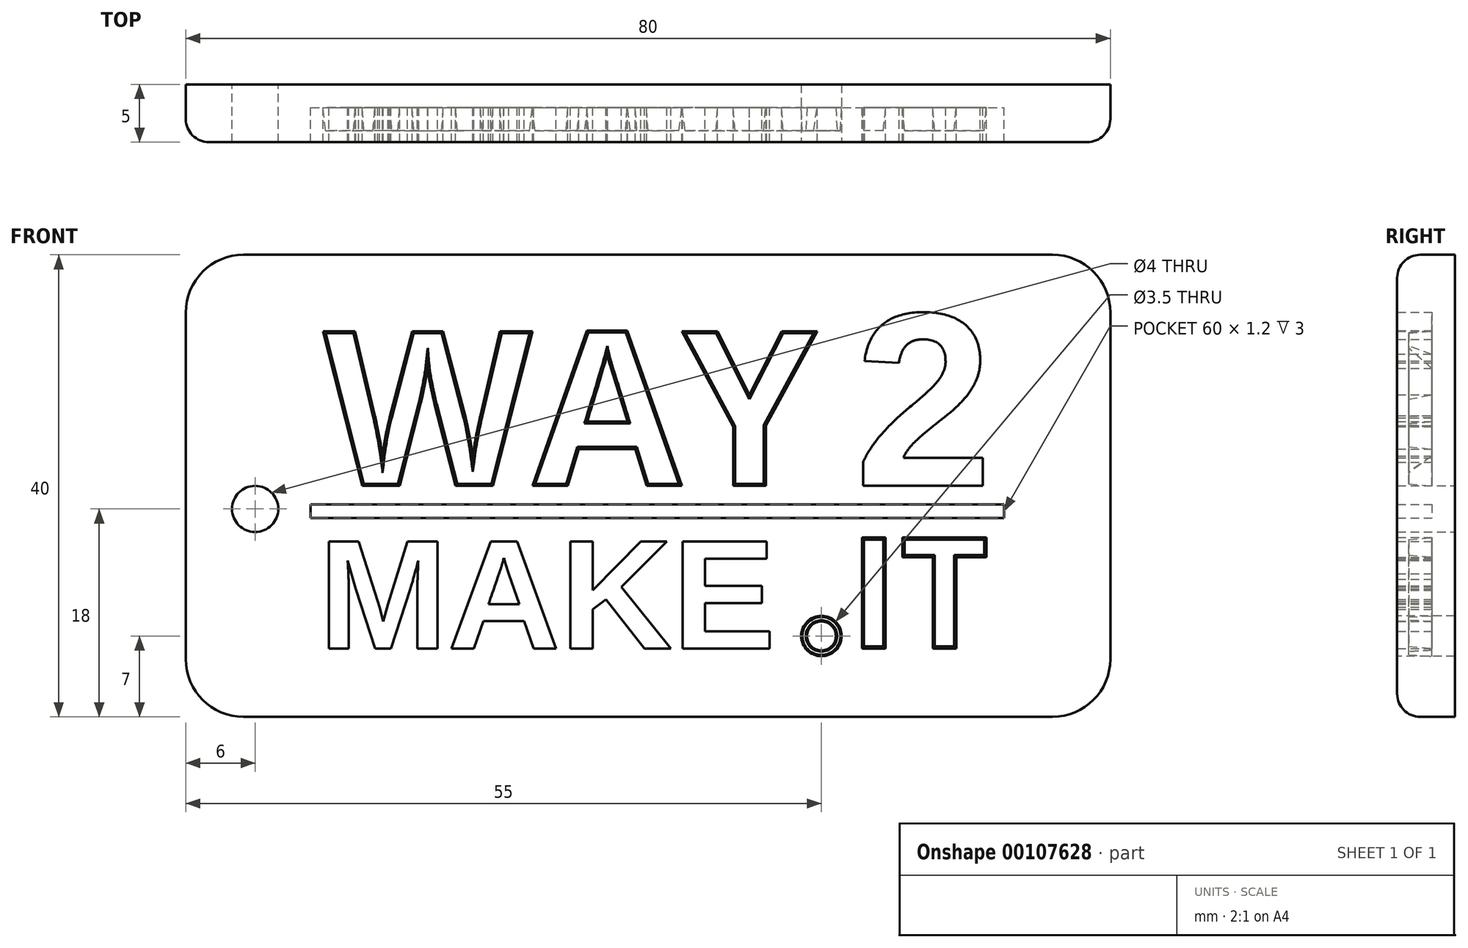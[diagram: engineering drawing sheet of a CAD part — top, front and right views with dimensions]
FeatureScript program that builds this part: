
annotation { "Feature Type Name" : "Feature", "Feature Type Description" : "" }
export const myFeature = defineFeature(function(context is Context, id is Id, definition is map)
    precondition{}
    {
        {
            var Q0;
            Q0=qCreatedBy(makeId("Front.planeOp"),FACE);
            var sketch = newSketch(context, id + "F0", { "sketchPlane" : qUnion([Q0])});
            skText(sketch, "E0", { "text": "WAY", "fontName": "OpenSans-Bold.ttf"});
            skText(sketch, "E1", { "text": "2", "fontName": "Arimo-Bold.ttf"});
            skText(sketch, "E2", { "text": "MAKE", "fontName": "Arimo-Bold.ttf"});
            skText(sketch, "E3", { "text": ".IT", "fontName": "OpenSans-Bold.ttf"});
            skLineSegment(sketch, "E4.bottom", {"start": v(-29.2, -1.6) * mm, "end": v(30.8, -1.6) * mm});
            skLineSegment(sketch, "E4.top", {"start": v(-29.2, -2.8) * mm, "end": v(30.8, -2.8) * mm});
            skLineSegment(sketch, "E4.left", {"start": v(-29.2, -1.6) * mm, "end": v(-29.2, -2.8) * mm});
            skLineSegment(sketch, "E4.right", {"start": v(30.8, -1.6) * mm, "end": v(30.8, -2.8) * mm});
            const initialGuessF0  = {"E0": [-0.02814, 0, 1, 0, 0.0135], "E1": [0.01786, 0, 1, 0, 0.0155], "E2": [-0.02853, -0.01408, 1, 0, 0.00968], "E3": [0.01347, -0.01408, 1, 0, 0.00968]};
            skSetInitialGuess(sketch, initialGuessF0);
            skSolve(sketch);
        }
        {
            var Q0;
            Q0=qCreatedBy(makeId("Front.planeOp"),FACE);
            var sketch = newSketch(context, id + "F1", { "sketchPlane" : qUnion([Q0])});
            skLineSegment(sketch, "E5.bottom", {"start": v(-40, 20) * mm, "end": v(40, 20) * mm});
            skLineSegment(sketch, "E5.top", {"start": v(-40, -20) * mm, "end": v(40, -20) * mm});
            skLineSegment(sketch, "E5.left", {"start": v(-40, 20) * mm, "end": v(-40, -20) * mm});
            skLineSegment(sketch, "E5.right", {"start": v(40, 20) * mm, "end": v(40, -20) * mm});
            skSolve(sketch);
        }
        {
            var Q0;
            Q0=makeQuery(id+"F1.imprint","IMPRINT",FACE,{"disambiguationData":[TD([[makeQuery(id+"F1.imprint","IMPRINT",EDGE,{"derivedFrom":sQuery(id+"F1.wireOp",EDGE,"E5.bottom")}),-1.0]])]});
            extrude(context, id + "F2", {"entities" : qUnion([Q0]), "oppositeDirection" : true, "depth" : 2 * mm, "offsetDistance" : 25 * mm});
        }
        {
            var Q0;
            Q0=qSketchRegion(id+"F1",true);
            extrude(context, id + "F3", {"entities" : qUnion([Q0]), "offsetDistance" : 25 * mm, "depth" : 3 * mm});
        }
        {
            var Q0;
            Q0=qSketchRegion(id+"F0",true);
            extrude(context, id + "F4", {"entities" : qUnion([Q0]), "operationType" : NewBodyOperationType.REMOVE, "offsetDistance" : 25 * mm, "depth" : 5 * mm});
        }
        {
            var Q0;
            Q0=makeQuery(id+"F0.imprint","IMPRINT",FACE,{"disambiguationData":[TD([[makeQuery(id+"F0.imprint","IMPRINT",EDGE,{"derivedFrom":sQuery(id+"F0.wireOp",EDGE,"E0.sketch_text.stroke-0")}),-1.0]])]});
            var Q1;
            Q1=makeQuery(id+"F0.imprint","IMPRINT",FACE,{"disambiguationData":[TD([[makeQuery(id+"F0.imprint","IMPRINT",EDGE,{"derivedFrom":sQuery(id+"F0.wireOp",EDGE,"E0.sketch_text.stroke-24")}),-1.0]])]});
            var Q2;
            Q2=makeQuery(id+"F0.imprint","IMPRINT",FACE,{"disambiguationData":[TD([[makeQuery(id+"F0.imprint","IMPRINT",EDGE,{"derivedFrom":sQuery(id+"F0.wireOp",EDGE,"E0.sketch_text.stroke-36")}),-1.0]])]});
            var Q3;
            Q3=makeQuery(id+"F0.imprint","IMPRINT",FACE,{"disambiguationData":[TD([[makeQuery(id+"F0.imprint","IMPRINT",EDGE,{"derivedFrom":sQuery(id+"F0.wireOp",EDGE,"E3.sketch_text.stroke-8")}),-1.0]])]});
            var Q4;
            Q4=makeQuery(id+"F0.imprint","IMPRINT",FACE,{"disambiguationData":[TD([[makeQuery(id+"F0.imprint","IMPRINT",EDGE,{"derivedFrom":sQuery(id+"F0.wireOp",EDGE,"E3.sketch_text.stroke-12")}),-1.0]])]});
            extrude(context, id + "F5", {"entities" : qUnion([Q0, Q1, Q2, Q3, Q4]), "operationType" : NewBodyOperationType.ADD, "depth" : 2 * mm, "offsetDistance" : 25 * mm, "hasDraft" : true, "draftAngle" : 5 * degree, "draftPullDirection" : true});
        }
        {
            var Q0;
            Q0=makeQuery(id+"F3.opExtrude","SWEPT_EDGE",EDGE,{"disambiguationData":[OSD([sQuery(id+"F1.wireOp",EDGE,"E5.top"),sQuery(id+"F1.wireOp",EDGE,"E5.right")])]});
            var Q1;
            Q1=makeQuery(id+"F3.opExtrude","SWEPT_EDGE",EDGE,{"disambiguationData":[OSD([sQuery(id+"F1.wireOp",EDGE,"E5.bottom"),sQuery(id+"F1.wireOp",EDGE,"E5.right")])]});
            var Q2;
            Q2=makeQuery(id+"F3.opExtrude","SWEPT_EDGE",EDGE,{"disambiguationData":[OSD([sQuery(id+"F1.wireOp",EDGE,"E5.top"),sQuery(id+"F1.wireOp",EDGE,"E5.left")])]});
            var Q3;
            Q3=makeQuery(id+"F3.opExtrude","SWEPT_EDGE",EDGE,{"disambiguationData":[OSD([sQuery(id+"F1.wireOp",EDGE,"E5.bottom"),sQuery(id+"F1.wireOp",EDGE,"E5.left")])]});
            var Q4;
            Q4=makeQuery(id+"F57l6EWdtboPAiu_6.opExtrude","SWEPT_EDGE",EDGE,{"disambiguationData":[OSD([sQuery(id+"F1.wireOp",EDGE,"E5.bottom"),sQuery(id+"F1.wireOp",EDGE,"E5.left")])]});
            var Q5;
            Q5=makeQuery(id+"F57l6EWdtboPAiu_6.opExtrude","SWEPT_EDGE",EDGE,{"disambiguationData":[OSD([sQuery(id+"F1.wireOp",EDGE,"E5.top"),sQuery(id+"F1.wireOp",EDGE,"E5.left")])]});
            var Q6;
            Q6=makeQuery(id+"F57l6EWdtboPAiu_6.opExtrude","SWEPT_EDGE",EDGE,{"disambiguationData":[OSD([sQuery(id+"F1.wireOp",EDGE,"E5.bottom"),sQuery(id+"F1.wireOp",EDGE,"E5.right")])]});
            var Q7;
            Q7=makeQuery(id+"F57l6EWdtboPAiu_6.opExtrude","SWEPT_EDGE",EDGE,{"disambiguationData":[OSD([sQuery(id+"F1.wireOp",EDGE,"E5.top"),sQuery(id+"F1.wireOp",EDGE,"E5.right")])]});
            var Q8;
            Q8=makeQuery(id+"F2.opExtrude","SWEPT_EDGE",EDGE,{"disambiguationData":[OSD([sQuery(id+"F1.wireOp",EDGE,"E5.top"),sQuery(id+"F1.wireOp",EDGE,"E5.left")])]});
            var Q9;
            Q9=makeQuery(id+"F2.opExtrude","SWEPT_EDGE",EDGE,{"disambiguationData":[OSD([sQuery(id+"F1.wireOp",EDGE,"E5.top"),sQuery(id+"F1.wireOp",EDGE,"E5.right")])]});
            var Q10;
            Q10=makeQuery(id+"F2.opExtrude","SWEPT_EDGE",EDGE,{"disambiguationData":[OSD([sQuery(id+"F1.wireOp",EDGE,"E5.bottom"),sQuery(id+"F1.wireOp",EDGE,"E5.right")])]});
            var Q11;
            Q11=makeQuery(id+"F2.opExtrude","SWEPT_EDGE",EDGE,{"disambiguationData":[OSD([sQuery(id+"F1.wireOp",EDGE,"E5.bottom"),sQuery(id+"F1.wireOp",EDGE,"E5.left")])]});
            fillet(context, id + "F6", {"entities" : qUnion([Q0, Q1, Q2, Q3, Q4, Q5, Q6, Q7, Q8, Q9, Q10, Q11]), "radius" : 5 * mm, "tangentPropagation" : true, "allowEdgeOverflow" : false});
        }
        {
            var Q0;
            Q0=qCreatedBy(makeId("Front.planeOp"),FACE);
            var sketch = newSketch(context, id + "F7", { "sketchPlane" : qUnion([Q0])});
            skCircle(sketch, "E6", {"center": v(-34, -2) * mm, "radius": 2 * mm});
            skSolve(sketch);
        }
        {
            var Q0;
            Q0=qSketchRegion(id+"F7",true);
            extrude(context, id + "F8", {"entities" : qUnion([Q0]), "operationType" : NewBodyOperationType.REMOVE, "endBound" : BoundingType.UP_TO_NEXT, "offsetDistance" : 25 * mm, "depth" : 25 * mm, "hasSecondDirection" : true, "secondDirectionOppositeDirection" : true, "secondDirectionDepth" : 25 * mm});
        }
        {
            var Q0;
            Q0=qCreatedBy(makeId("Front.planeOp"),FACE);
            var sketch = newSketch(context, id + "F9", { "sketchPlane" : qUnion([Q0])});
            skCircle(sketch, "E7", {"center": v(15, -13) * mm, "radius": 1.75 * mm});
            skCircle(sketch, "E8", {"center": v(15, -13) * mm, "radius": 1.25 * mm});
            skSolve(sketch);
        }
        {
            var Q0;
            Q0=makeQuery(id+"F9.imprint","IMPRINT",FACE,{"disambiguationData":[TD([[makeQuery(id+"F9.imprint","IMPRINT",EDGE,{"derivedFrom":sQuery(id+"F9.wireOp",EDGE,"E7")}),1.0]])]});
            var Q1;
            Q1=makeQuery(id+"F9.imprint","IMPRINT",FACE,{"disambiguationData":[TD([[makeQuery(id+"F9.imprint","IMPRINT",EDGE,{"derivedFrom":sQuery(id+"F9.wireOp",EDGE,"E8")}),1.0]])]});
            extrude(context, id + "F10", {"entities" : qUnion([Q0, Q1]), "operationType" : NewBodyOperationType.REMOVE, "endBound" : BoundingType.SYMMETRIC, "oppositeDirection" : true, "depth" : 50 * mm, "offsetDistance" : 25 * mm});
        }
        {
            var Q0;
            Q0=makeQuery(id+"F9.imprint","IMPRINT",FACE,{"disambiguationData":[TD([[makeQuery(id+"F9.imprint","IMPRINT",EDGE,{"derivedFrom":sQuery(id+"F9.wireOp",EDGE,"E7")}),1.0]])]});
            extrude(context, id + "F11", {"entities" : qUnion([Q0]), "operationType" : NewBodyOperationType.ADD, "depth" : 2 * mm, "offsetDistance" : 25 * mm, "hasDraft" : true, "draftAngle" : 3 * degree, "draftPullDirection" : true});
        }
        {
            var Q0;
            Q0=makeQuery(id+"F9.imprint","IMPRINT",FACE,{"disambiguationData":[TD([[makeQuery(id+"F9.imprint","IMPRINT",EDGE,{"derivedFrom":sQuery(id+"F9.wireOp",EDGE,"E8")}),1.0]])]});
            extrude(context, id + "F12", {"entities" : qUnion([Q0]), "operationType" : NewBodyOperationType.REMOVE, "oppositeDirection" : true, "depth" : 25 * mm, "offsetDistance" : 25 * mm});
        }
        {
            var Q0;
            Q0=makeQuery(id+"F3.opExtrude","CAP_EDGE",EDGE,{"disambiguationData":[OSD([sQuery(id+"F1.wireOp",EDGE,"E5.left")])],"isStart":false});
            var Q1;
            {var subQ0=sQuery(id+"F1.wireOp",EDGE,"E5.left");var subQ1=sQuery(id+"F1.wireOp",EDGE,"E5.top");var subQ2=sQuery(id+"F1.wireOp",EDGE,"E5.right");var subQ3=sQuery(id+"F1.wireOp",EDGE,"E5.bottom");Q1=makeQuery(id+"F6.opFillet","BLEND_EDGE",EDGE,{"blendedFrom":[makeQuery(id+"F3.opExtrude","SWEPT_EDGE",EDGE,{"disambiguationData":[OSD([subQ3,subQ0])]}),makeQuery(id+"F4.boolean.opBoolean","SPLIT",FACE,{"disambiguationData":[TD([makeQuery(id+"F3.opExtrude","SWEPT_FACE",FACE,{"disambiguationData":[OSD([subQ3])]})])],"derivedFrom":makeQuery(id+"F3.opExtrude","CAP_FACE",FACE,{"disambiguationData":[OSD([subQ3,subQ1,subQ0,subQ2])],"isStart":false})})],"blendedInto":[makeQuery(id+"F4.boolean.opBoolean","SPLIT",FACE,{"disambiguationData":[TD([makeQuery(id+"F3.opExtrude","SWEPT_FACE",FACE,{"disambiguationData":[OSD([subQ3])]})])],"derivedFrom":makeQuery(id+"F3.opExtrude","CAP_FACE",FACE,{"disambiguationData":[OSD([subQ3,subQ1,subQ0,subQ2])],"isStart":false})})]});}
            var Q2;
            Q2=makeQuery(id+"F3.opExtrude","CAP_EDGE",EDGE,{"disambiguationData":[OSD([sQuery(id+"F1.wireOp",EDGE,"E5.bottom")])],"isStart":false});
            var Q3;
            {var subQ0=sQuery(id+"F1.wireOp",EDGE,"E5.left");var subQ1=sQuery(id+"F1.wireOp",EDGE,"E5.top");var subQ2=sQuery(id+"F1.wireOp",EDGE,"E5.right");var subQ3=sQuery(id+"F1.wireOp",EDGE,"E5.bottom");Q3=makeQuery(id+"F6.opFillet","BLEND_EDGE",EDGE,{"blendedFrom":[makeQuery(id+"F3.opExtrude","SWEPT_EDGE",EDGE,{"disambiguationData":[OSD([subQ3,subQ2])]}),makeQuery(id+"F4.boolean.opBoolean","SPLIT",FACE,{"disambiguationData":[TD([makeQuery(id+"F3.opExtrude","SWEPT_FACE",FACE,{"disambiguationData":[OSD([subQ3])]})])],"derivedFrom":makeQuery(id+"F3.opExtrude","CAP_FACE",FACE,{"disambiguationData":[OSD([subQ3,subQ1,subQ0,subQ2])],"isStart":false})})],"blendedInto":[makeQuery(id+"F4.boolean.opBoolean","SPLIT",FACE,{"disambiguationData":[TD([makeQuery(id+"F3.opExtrude","SWEPT_FACE",FACE,{"disambiguationData":[OSD([subQ3])]})])],"derivedFrom":makeQuery(id+"F3.opExtrude","CAP_FACE",FACE,{"disambiguationData":[OSD([subQ3,subQ1,subQ0,subQ2])],"isStart":false})})]});}
            var Q4;
            Q4=makeQuery(id+"F3.opExtrude","CAP_EDGE",EDGE,{"disambiguationData":[OSD([sQuery(id+"F1.wireOp",EDGE,"E5.right")])],"isStart":false});
            var Q5;
            {var subQ0=sQuery(id+"F1.wireOp",EDGE,"E5.left");var subQ1=sQuery(id+"F1.wireOp",EDGE,"E5.top");var subQ2=sQuery(id+"F1.wireOp",EDGE,"E5.right");var subQ3=sQuery(id+"F1.wireOp",EDGE,"E5.bottom");Q5=makeQuery(id+"F6.opFillet","BLEND_EDGE",EDGE,{"blendedFrom":[makeQuery(id+"F3.opExtrude","SWEPT_EDGE",EDGE,{"disambiguationData":[OSD([subQ1,subQ2])]}),makeQuery(id+"F4.boolean.opBoolean","SPLIT",FACE,{"disambiguationData":[TD([makeQuery(id+"F3.opExtrude","SWEPT_FACE",FACE,{"disambiguationData":[OSD([subQ3])]})])],"derivedFrom":makeQuery(id+"F3.opExtrude","CAP_FACE",FACE,{"disambiguationData":[OSD([subQ3,subQ1,subQ0,subQ2])],"isStart":false})})],"blendedInto":[makeQuery(id+"F4.boolean.opBoolean","SPLIT",FACE,{"disambiguationData":[TD([makeQuery(id+"F3.opExtrude","SWEPT_FACE",FACE,{"disambiguationData":[OSD([subQ3])]})])],"derivedFrom":makeQuery(id+"F3.opExtrude","CAP_FACE",FACE,{"disambiguationData":[OSD([subQ3,subQ1,subQ0,subQ2])],"isStart":false})})]});}
            var Q6;
            Q6=makeQuery(id+"F3.opExtrude","CAP_EDGE",EDGE,{"disambiguationData":[OSD([sQuery(id+"F1.wireOp",EDGE,"E5.top")])],"isStart":false});
            var Q7;
            {var subQ0=sQuery(id+"F1.wireOp",EDGE,"E5.left");var subQ1=sQuery(id+"F1.wireOp",EDGE,"E5.top");var subQ2=sQuery(id+"F1.wireOp",EDGE,"E5.right");var subQ3=sQuery(id+"F1.wireOp",EDGE,"E5.bottom");Q7=makeQuery(id+"F6.opFillet","BLEND_EDGE",EDGE,{"blendedFrom":[makeQuery(id+"F3.opExtrude","SWEPT_EDGE",EDGE,{"disambiguationData":[OSD([subQ1,subQ0])]}),makeQuery(id+"F4.boolean.opBoolean","SPLIT",FACE,{"disambiguationData":[TD([makeQuery(id+"F3.opExtrude","SWEPT_FACE",FACE,{"disambiguationData":[OSD([subQ3])]})])],"derivedFrom":makeQuery(id+"F3.opExtrude","CAP_FACE",FACE,{"disambiguationData":[OSD([subQ3,subQ1,subQ0,subQ2])],"isStart":false})})],"blendedInto":[makeQuery(id+"F4.boolean.opBoolean","SPLIT",FACE,{"disambiguationData":[TD([makeQuery(id+"F3.opExtrude","SWEPT_FACE",FACE,{"disambiguationData":[OSD([subQ3])]})])],"derivedFrom":makeQuery(id+"F3.opExtrude","CAP_FACE",FACE,{"disambiguationData":[OSD([subQ3,subQ1,subQ0,subQ2])],"isStart":false})})]});}
            fillet(context, id + "F13", {"entities" : qUnion([Q0, Q1, Q2, Q3, Q4, Q5, Q6, Q7]), "radius" : 2 * mm, "tangentPropagation" : true, "allowEdgeOverflow" : false});
        }
    });
